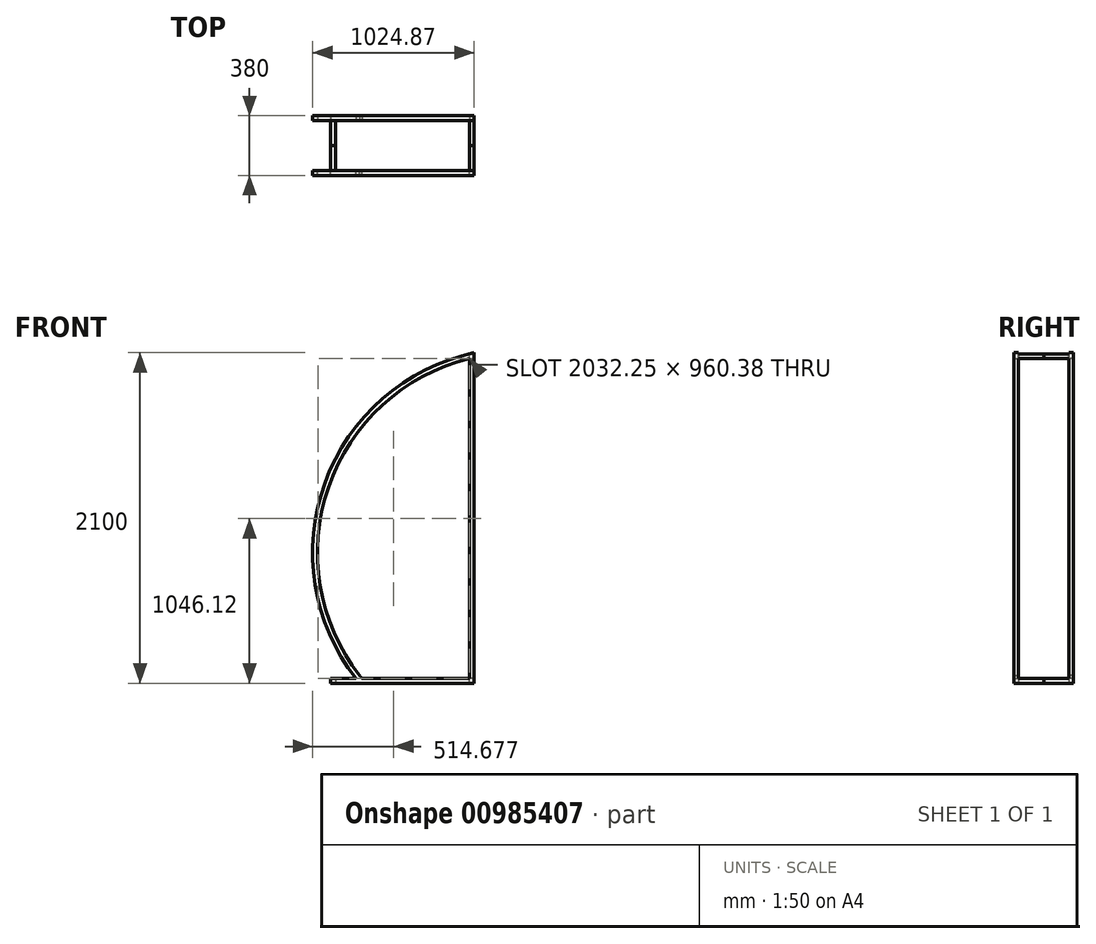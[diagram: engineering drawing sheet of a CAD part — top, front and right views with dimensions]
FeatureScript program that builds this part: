
annotation { "Feature Type Name" : "Feature", "Feature Type Description" : "" }
export const myFeature = defineFeature(function(context is Context, id is Id, definition is map)
    precondition{}
    {
        {
            var Q0;
            Q0=qCreatedBy(makeId("Front.planeOp"),FACE);
            var sketch = newSketch(context, id + "F0", { "sketchPlane" : qUnion([Q0])});
            skLineSegment(sketch, "E0", {"start": v(-650.02, 1141.99) * mm, "end": v(-650.02, -958.01) * mm});
            skLineSegment(sketch, "E1", {"start": v(-650.02, -958.01) * mm, "end": v(-1560.02, -958.01) * mm});
            skLineSegment(sketch, "E2", {"start": v(-1560.02, -958.01) * mm, "end": v(-1560.02, -928.01) * mm});
            skArc(sketch, "E3", {"start": v(-650.02, 1141.99) * mm, "mid": v(-1597.14, 314.28) * mm, "end": v(-1400.02, -928.01) * mm});
            skArc(sketch, "E4.0", {"start": v(-680.02, 1104.24) * mm, "mid": v(-1575.16, 286.47) * mm, "end": v(-1376.36, -909.56) * mm});
            skLineSegment(sketch, "E4.1", {"start": v(-680.02, 1104.24) * mm, "end": v(-680.02, -928.01) * mm});
            skLineSegment(sketch, "E5.0", {"start": v(-680.02, -928.01) * mm, "end": v(-1362.2, -928.01) * mm});
            skArc(sketch, "E6", {"start": v(-1376.36, -909.56) * mm, "mid": v(-1369.32, -918.82) * mm, "end": v(-1362.2, -928.01) * mm});
            skLineSegment(sketch, "E7.trimOffspring", {"start": v(-1400.02, -928.01) * mm, "end": v(-1560.02, -928.01) * mm});
            skSolve(sketch);
        }
        {
            var Q0;
            Q0=makeQuery(id+"F0.imprint","IMPRINT",FACE,{"disambiguationData":[TD([[makeQuery(id+"F0.imprint","IMPRINT",EDGE,{"derivedFrom":sQuery(id+"F0.wireOp",EDGE,"E0")}),-1.0]])]});
            extrude(context, id + "F1", {"entities" : qUnion([Q0]), "depth" : 190 * mm, "offsetDistance" : 25 * mm, "hasSecondDirection" : true, "secondDirectionOppositeDirection" : false, "secondDirectionDepth" : 160 * mm});
        }
        {
            var Q0;
            Q0=makeQuery(id+"F1.opExtrude","CAP_FACE",FACE,{"disambiguationData":[OSD([sQuery(id+"F0.wireOp",EDGE,"E0"),sQuery(id+"F0.wireOp",EDGE,"E1"),sQuery(id+"F0.wireOp",EDGE,"E2"),sQuery(id+"F0.wireOp",EDGE,"E3"),sQuery(id+"F0.wireOp",EDGE,"E4.0"),sQuery(id+"F0.wireOp",EDGE,"E4.1"),sQuery(id+"F0.wireOp",EDGE,"E5.0"),sQuery(id+"F0.wireOp",EDGE,"E6"),sQuery(id+"F0.wireOp",EDGE,"E7.trimOffspring")])],"isStart":true});
            var sketch = newSketch(context, id + "F2", { "sketchPlane" : qUnion([Q0])});
            skLineSegment(sketch, "E8.bottom", {"start": v(680.02, 1104.24) * mm, "end": v(650.02, 1104.24) * mm});
            skLineSegment(sketch, "E8.top", {"start": v(680.02, 1134.24) * mm, "end": v(650.02, 1134.24) * mm});
            skLineSegment(sketch, "E8.left", {"start": v(680.02, 1104.24) * mm, "end": v(680.02, 1134.24) * mm});
            skLineSegment(sketch, "E8.right", {"start": v(650.02, 1104.24) * mm, "end": v(650.02, 1134.24) * mm});
            skLineSegment(sketch, "E9.bottom", {"start": v(650.02, -958.01) * mm, "end": v(680.02, -958.01) * mm});
            skLineSegment(sketch, "E9.top", {"start": v(650.02, -928.01) * mm, "end": v(680.02, -928.01) * mm});
            skLineSegment(sketch, "E9.left", {"start": v(650.02, -958.01) * mm, "end": v(650.02, -928.01) * mm});
            skLineSegment(sketch, "E9.right", {"start": v(680.02, -958.01) * mm, "end": v(680.02, -928.01) * mm});
            skLineSegment(sketch, "E10.bottom", {"start": v(1560.02, -928.01) * mm, "end": v(1530.02, -928.01) * mm});
            skLineSegment(sketch, "E10.top", {"start": v(1560.02, -958.01) * mm, "end": v(1530.02, -958.01) * mm});
            skLineSegment(sketch, "E10.left", {"start": v(1560.02, -928.01) * mm, "end": v(1560.02, -958.01) * mm});
            skLineSegment(sketch, "E10.right", {"start": v(1530.02, -928.01) * mm, "end": v(1530.02, -958.01) * mm});
            skSolve(sketch);
        }
        {
            var Q0;
            Q0=makeQuery(id+"F2.imprint","IMPRINT",FACE,{"disambiguationData":[TD([[makeQuery(id+"F2.imprint","IMPRINT",EDGE,{"derivedFrom":sQuery(id+"F2.wireOp",EDGE,"E10.bottom")}),-1.0]])]});
            var Q1;
            Q1=makeQuery(id+"F2.imprint","IMPRINT",FACE,{"disambiguationData":[TD([[makeQuery(id+"F2.imprint","IMPRINT",EDGE,{"derivedFrom":sQuery(id+"F2.wireOp",EDGE,"E9.bottom")}),1.0]])]});
            var Q2;
            Q2=makeQuery(id+"F2.imprint","IMPRINT",FACE,{"disambiguationData":[TD([[makeQuery(id+"F2.imprint","IMPRINT",EDGE,{"derivedFrom":sQuery(id+"F2.wireOp",EDGE,"E8.bottom")}),-1.0]])]});
            extrude(context, id + "F3", {"entities" : qUnion([Q0, Q1, Q2]), "operationType" : NewBodyOperationType.ADD, "depth" : 160 * mm, "offsetDistance" : 25 * mm});
        }
        {
            var Q0;
            Q0=makeQuery(id+"F1.opExtrude","SWEPT_BODY",BODY,{"disambiguationData":[OSD([sQuery(id+"F0.wireOp",EDGE,"97fa6f72-d368-4bea-88e0-9f5cc636653a"),sQuery(id+"F0.wireOp",EDGE,"E0"),sQuery(id+"F0.wireOp",EDGE,"zRGcRb5l-WhYl-2FFL-i8dd-t34RehFeJWZk"),sQuery(id+"F0.wireOp",EDGE,"c7f607c3-8893-41fd-a439-ea40ffdb8eb8.0"),sQuery(id+"F0.wireOp",EDGE,"c7f607c3-8893-41fd-a439-ea40ffdb8eb8.1"),sQuery(id+"F0.wireOp",EDGE,"c7f607c3-8893-41fd-a439-ea40ffdb8eb8.2"),sQuery(id+"F0.wireOp",EDGE,"lT0X2mwb-oEVM-9NtA-zBRs-CK7Scm6XKRi0"),sQuery(id+"F0.wireOp",EDGE,"3oa2Q9Fb-nToq-qSJS-JCCg-ilBdUlJ1RMia"),sQuery(id+"F0.wireOp",EDGE,"9RPrAjXz-fnB6-APnK-Qqak-Op5x7xOsiAd9")])]});
            var Q1;
            Q1=qCreatedBy(makeId("Front.planeOp"),FACE);
            mirror(context, id + "F4", {"entities" : qUnion([Q0]), "mirrorPlane" : qUnion([Q1])});
        }
        {
            var Q0;
            Q0=makeQuery(id+"F4.opPattern","COPY",FACE,{"derivedFrom":makeQuery(id+"F1.opExtrude","CAP_FACE",FACE,{"disambiguationData":[OSD([sQuery(id+"F0.wireOp",EDGE,"E0"),sQuery(id+"F0.wireOp",EDGE,"E1"),sQuery(id+"F0.wireOp",EDGE,"E2"),sQuery(id+"F0.wireOp",EDGE,"E3"),sQuery(id+"F0.wireOp",EDGE,"E4.0"),sQuery(id+"F0.wireOp",EDGE,"E4.1"),sQuery(id+"F0.wireOp",EDGE,"E5.0"),sQuery(id+"F0.wireOp",EDGE,"E6"),sQuery(id+"F0.wireOp",EDGE,"E7.trimOffspring")])],"isStart":false}),"instanceName":"1"});
            var sketch = newSketch(context, id + "F5", { "sketchPlane" : qUnion([Q0])});
            skLineSegment(sketch, "E11", {"start": v(650.02, 690.6) * mm, "end": v(1345.4, 690.6) * mm});
            skLineSegment(sketch, "E12", {"start": v(1345.4, 690.6) * mm, "end": v(1345.4, 670.6) * mm});
            skLineSegment(sketch, "E13", {"start": v(1345.4, 670.6) * mm, "end": v(650.02, 670.6) * mm});
            skLineSegment(sketch, "E14", {"start": v(650.02, 670.6) * mm, "end": v(650.02, 690.6) * mm});
            skLineSegment(sketch, "E15", {"start": v(650.02, 151.4) * mm, "end": v(1613.65, 151.4) * mm});
            skLineSegment(sketch, "E16", {"start": v(650.02, -389.57) * mm, "end": v(1617.78, -389.57) * mm});
            skSolve(sketch);
        }
    });
